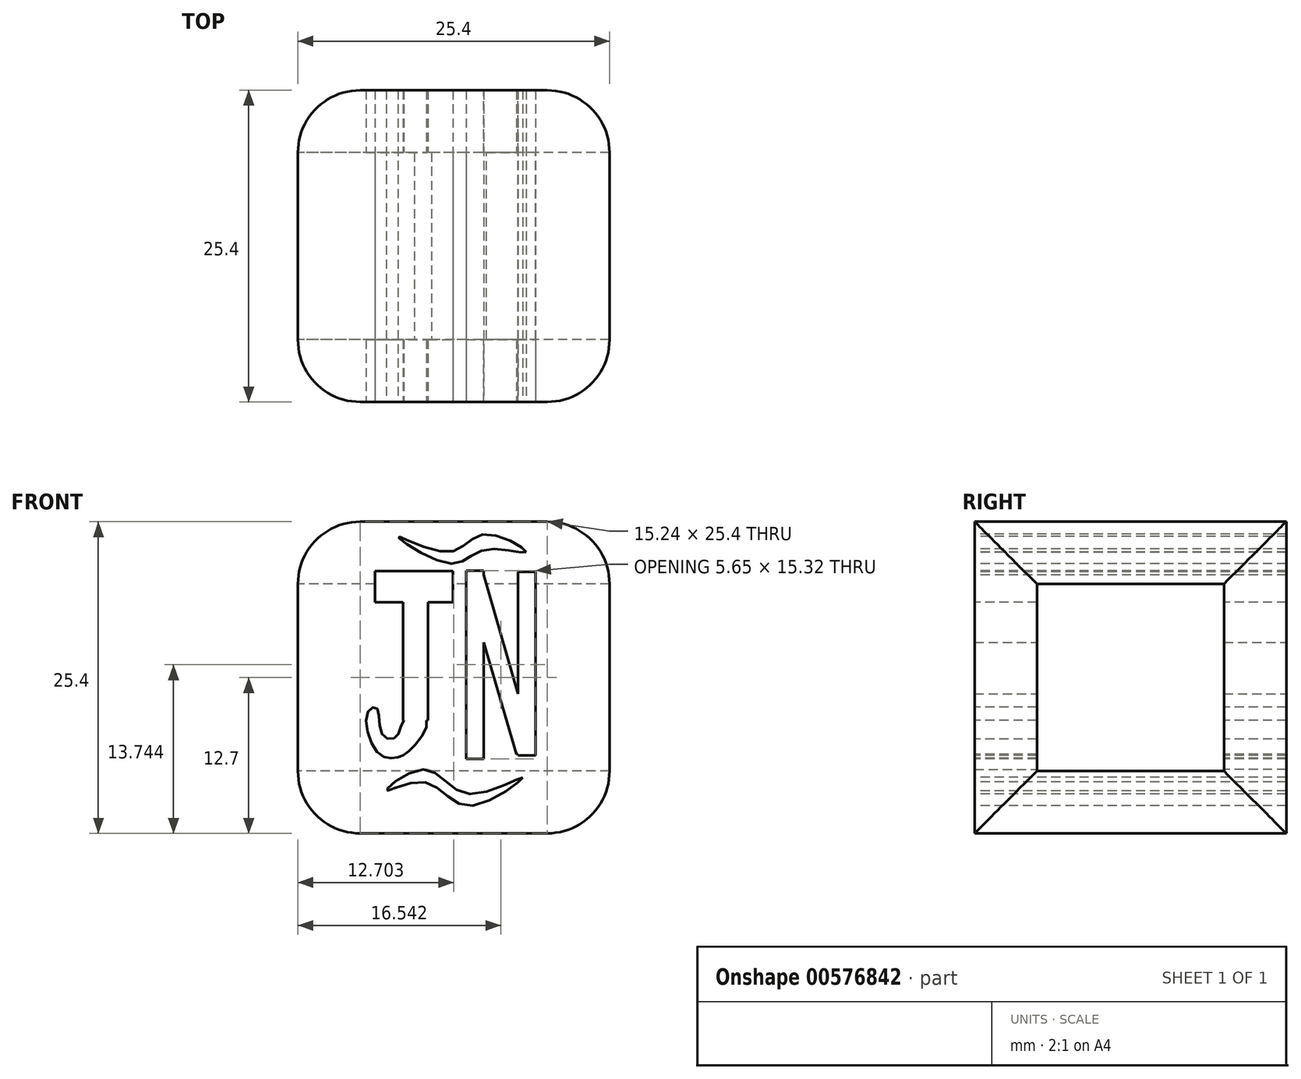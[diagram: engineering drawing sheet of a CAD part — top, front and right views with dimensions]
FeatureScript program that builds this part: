
annotation { "Feature Type Name" : "Feature", "Feature Type Description" : "" }
export const myFeature = defineFeature(function(context is Context, id is Id, definition is map)
    precondition{}
    {
        {
            var Q0;
            Q0=qCreatedBy(makeId("Front.planeOp"),FACE);
            var sketch = newSketch(context, id + "F0", { "sketchPlane" : qUnion([Q0])});
            skLineSegment(sketch, "E0.bottom", {"start": v(-49.84, 43.23) * mm, "end": v(-24.44, 43.23) * mm});
            skLineSegment(sketch, "E0.top", {"start": v(-49.84, 17.83) * mm, "end": v(-24.44, 17.83) * mm});
            skLineSegment(sketch, "E0.left", {"start": v(-49.84, 43.23) * mm, "end": v(-49.84, 17.83) * mm});
            skLineSegment(sketch, "E0.right", {"start": v(-24.44, 43.23) * mm, "end": v(-24.44, 17.83) * mm});
            skSolve(sketch);
        }
        {
            var Q0;
            Q0=makeQuery(id+"F0.imprint","IMPRINT",FACE,{"disambiguationData":[TD([[makeQuery(id+"F0.imprint","IMPRINT",EDGE,{"derivedFrom":sQuery(id+"F0.wireOp",EDGE,"E0.bottom")}),-1.0]])]});
            extrude(context, id + "F1", {"entities" : qUnion([Q0]), "depth" : 25.4 * mm, "offsetDistance" : 25.4 * mm});
        }
        {
            var Q0;
            Q0=makeQuery(id+"F1.opExtrude","SWEPT_FACE",FACE,{"disambiguationData":[OSD([sQuery(id+"F0.wireOp",EDGE,"E0.left")])]});
            var Q1;
            Q1=makeQuery(id+"F1.opExtrude","SWEPT_FACE",FACE,{"disambiguationData":[OSD([sQuery(id+"F0.wireOp",EDGE,"E0.right")])]});
            fillet(context, id + "F2", {"entities" : qUnion([Q0, Q1]), "radius" : 5.08 * mm, "tangentPropagation" : true, "allowEdgeOverflow" : false});
        }
        {
            var Q0;
            Q0=makeQuery(id+"F1.opExtrude","SWEPT_FACE",FACE,{"disambiguationData":[OSD([sQuery(id+"F0.wireOp",EDGE,"E0.left")])]});
            extrude(context, id + "F3", {"entities" : qUnion([Q0]), "operationType" : NewBodyOperationType.REMOVE, "endBound" : BoundingType.THROUGH_ALL, "oppositeDirection" : true, "depth" : 25.4 * mm, "offsetDistance" : 25.4 * mm});
        }
        {
            var Q0;
            Q0=makeQuery(id+"F1.opExtrude","CAP_FACE",FACE,{"disambiguationData":[OSD([sQuery(id+"F0.wireOp",EDGE,"E0.bottom"),sQuery(id+"F0.wireOp",EDGE,"E0.top"),sQuery(id+"F0.wireOp",EDGE,"E0.left"),sQuery(id+"F0.wireOp",EDGE,"E0.right")])],"isStart":false});
            var sketch = newSketch(context, id + "F4", { "sketchPlane" : qUnion([Q0])});
            skLineSegment(sketch, "E1.bottom", {"start": v(-43.56, 39.2) * mm, "end": v(-37.2, 39.2) * mm});
            skLineSegment(sketch, "E1.top", {"start": v(-43.56, 36.66) * mm, "end": v(-37.2, 36.66) * mm});
            skLineSegment(sketch, "E1.left", {"start": v(-43.56, 39.2) * mm, "end": v(-43.56, 36.66) * mm});
            skLineSegment(sketch, "E1.right", {"start": v(-37.2, 39.2) * mm, "end": v(-37.2, 36.66) * mm});
            skSolve(sketch);
        }
        {
            var Q0;
            Q0=makeQuery(id+"F4.imprint","IMPRINT",FACE,{"disambiguationData":[TD([[makeQuery(id+"F4.imprint","IMPRINT",EDGE,{"derivedFrom":sQuery(id+"F4.wireOp",EDGE,"E1.bottom")}),1.0]])]});
            var sketch = newSketch(context, id + "F5", { "sketchPlane" : qUnion([Q0])});
            skLineSegment(sketch, "E2.bottom", {"start": v(-41.26, 36.7) * mm, "end": v(-39.22, 36.7) * mm});
            skLineSegment(sketch, "E2.top", {"start": v(-41.26, 27.05) * mm, "end": v(-39.22, 27.05) * mm});
            skLineSegment(sketch, "E2.left", {"start": v(-41.26, 36.7) * mm, "end": v(-41.26, 27.05) * mm});
            skLineSegment(sketch, "E2.right", {"start": v(-39.22, 36.7) * mm, "end": v(-39.22, 27.05) * mm});
            skSolve(sketch);
        }
        {
            var Q0;
            Q0=makeQuery(id+"F4.imprint","IMPRINT",FACE,{"disambiguationData":[TD([[makeQuery(id+"F4.imprint","IMPRINT",EDGE,{"derivedFrom":sQuery(id+"F4.wireOp",EDGE,"E1.bottom")}),-1.0]])]});
            extrude(context, id + "F6", {"entities" : qUnion([Q0]), "operationType" : NewBodyOperationType.REMOVE, "oppositeDirection" : true, "depth" : 25.4 * mm, "offsetDistance" : 25.4 * mm});
        }
        {
            var Q0;
            {var subQ0=sQuery(id+"F5.wireOp",EDGE,"E2.top");Q0=makeQuery(id+"F5.imprint","IMPRINT",FACE,{"disambiguationData":[TD([[makeQuery(id+"F5.imprint","IMPRINT",EDGE,{"derivedFrom":subQ0}),1.0]])]});}
            extrude(context, id + "F7", {"entities" : qUnion([Q0]), "operationType" : NewBodyOperationType.REMOVE, "oppositeDirection" : true, "depth" : 25.4 * mm, "offsetDistance" : 25.4 * mm});
        }
        {
            var Q0;
            Q0=makeQuery(id+"F4.imprint","IMPRINT",FACE,{"disambiguationData":[TD([[makeQuery(id+"F4.imprint","IMPRINT",EDGE,{"derivedFrom":sQuery(id+"F4.wireOp",EDGE,"E1.bottom")}),1.0]])]});
            var sketch = newSketch(context, id + "F8", { "sketchPlane" : qUnion([Q0])});
            skFitSpline(sketch, "E3", {"points": [v(-39.38, 27.07) * mm, v(-41.1, 27.17) * mm, v(-41.77, 25.73) * mm, v(-42.92, 25.83) * mm, v(-43.4, 28.03) * mm, v(-44.17, 27.65) * mm, v(-43.3, 24.4) * mm, v(-41.77, 24) * mm, v(-40.53, 24.77) * mm, v(-39.38, 27.07) * mm]});
            skSolve(sketch);
        }
        {
            var Q0;
            Q0=makeQuery(id+"F4.imprint","IMPRINT",FACE,{"disambiguationData":[TD([[makeQuery(id+"F4.imprint","IMPRINT",EDGE,{"derivedFrom":sQuery(id+"F4.wireOp",EDGE,"E1.bottom")}),1.0]])]});
            var sketch = newSketch(context, id + "F9", { "sketchPlane" : qUnion([Q0])});
            skLineSegment(sketch, "E4.bottom", {"start": v(-36.12, 39.24) * mm, "end": v(-34.69, 39.24) * mm});
            skLineSegment(sketch, "E4.top", {"start": v(-36.12, 23.91) * mm, "end": v(-34.69, 23.91) * mm});
            skLineSegment(sketch, "E4.left", {"start": v(-36.12, 39.24) * mm, "end": v(-36.12, 23.91) * mm});
            skLineSegment(sketch, "E4.right", {"start": v(-34.69, 39.24) * mm, "end": v(-34.69, 23.91) * mm});
            skSolve(sketch);
        }
        {
            var Q0;
            Q0=makeQuery(id+"F4.imprint","IMPRINT",FACE,{"disambiguationData":[TD([[makeQuery(id+"F4.imprint","IMPRINT",EDGE,{"derivedFrom":sQuery(id+"F4.wireOp",EDGE,"E1.bottom")}),1.0]])]});
            var sketch = newSketch(context, id + "F10", { "sketchPlane" : qUnion([Q0])});
            skLineSegment(sketch, "E5", {"start": v(-34.77, 39.16) * mm, "end": v(-35.9, 37.55) * mm});
            skLineSegment(sketch, "E6", {"start": v(-35.9, 37.55) * mm, "end": v(-32.02, 24.27) * mm});
            skLineSegment(sketch, "E7", {"start": v(-32.02, 24.27) * mm, "end": v(-30.5, 24.27) * mm});
            skLineSegment(sketch, "E8", {"start": v(-30.5, 24.27) * mm, "end": v(-34.77, 39.16) * mm});
            skSolve(sketch);
        }
        {
            var Q0;
            Q0=makeQuery(id+"F4.imprint","IMPRINT",FACE,{"disambiguationData":[TD([[makeQuery(id+"F4.imprint","IMPRINT",EDGE,{"derivedFrom":sQuery(id+"F4.wireOp",EDGE,"E1.bottom")}),1.0]])]});
            var sketch = newSketch(context, id + "F11", { "sketchPlane" : qUnion([Q0])});
            skLineSegment(sketch, "E9.bottom", {"start": v(-31.9, 24.2) * mm, "end": v(-30.47, 24.2) * mm});
            skLineSegment(sketch, "E9.top", {"start": v(-31.9, 39.14) * mm, "end": v(-30.47, 39.14) * mm});
            skLineSegment(sketch, "E9.left", {"start": v(-31.9, 24.2) * mm, "end": v(-31.9, 39.14) * mm});
            skLineSegment(sketch, "E9.right", {"start": v(-30.47, 24.2) * mm, "end": v(-30.47, 39.14) * mm});
            skSolve(sketch);
        }
        {
            var Q0;
            Q0=makeQuery(id+"F10.imprint","IMPRINT",FACE,{"disambiguationData":[TD([[makeQuery(id+"F10.imprint","IMPRINT",EDGE,{"derivedFrom":sQuery(id+"F10.wireOp",EDGE,"E5")}),1.0]])]});
            extrude(context, id + "F12", {"entities" : qUnion([Q0]), "operationType" : NewBodyOperationType.REMOVE, "oppositeDirection" : true, "depth" : 25.4 * mm, "offsetDistance" : 25.4 * mm});
        }
        {
            var Q0;
            Q0=makeQuery(id+"F11.imprint","IMPRINT",FACE,{"disambiguationData":[TD([[makeQuery(id+"F11.imprint","IMPRINT",EDGE,{"derivedFrom":sQuery(id+"F11.wireOp",EDGE,"E9.bottom")}),1.0]])]});
            extrude(context, id + "F13", {"entities" : qUnion([Q0]), "operationType" : NewBodyOperationType.REMOVE, "oppositeDirection" : true, "depth" : 25.4 * mm, "offsetDistance" : 25.4 * mm});
        }
        {
            var Q0;
            Q0=makeQuery(id+"F9.imprint","IMPRINT",FACE,{"disambiguationData":[TD([[makeQuery(id+"F9.imprint","IMPRINT",EDGE,{"derivedFrom":sQuery(id+"F9.wireOp",EDGE,"E4.bottom")}),-1.0]])]});
            extrude(context, id + "F14", {"entities" : qUnion([Q0]), "operationType" : NewBodyOperationType.REMOVE, "oppositeDirection" : true, "depth" : 25.4 * mm, "offsetDistance" : 25.4 * mm});
        }
        {
            var Q0;
            Q0=makeQuery(id+"F8.imprint","IMPRINT",FACE,{"disambiguationData":[TD([[makeQuery(id+"F8.imprint","IMPRINT",EDGE,{"derivedFrom":sQuery(id+"F8.wireOp",EDGE,"E3")}),1.0]])]});
            extrude(context, id + "F15", {"entities" : qUnion([Q0]), "operationType" : NewBodyOperationType.REMOVE, "oppositeDirection" : true, "depth" : 25.4 * mm, "offsetDistance" : 25.4 * mm});
        }
        {
            var Q0;
            Q0=makeQuery(id+"F4.imprint","IMPRINT",FACE,{"disambiguationData":[TD([[makeQuery(id+"F4.imprint","IMPRINT",EDGE,{"derivedFrom":sQuery(id+"F4.wireOp",EDGE,"E1.bottom")}),1.0]])]});
            var sketch = newSketch(context, id + "F16", { "sketchPlane" : qUnion([Q0])});
            skFitSpline(sketch, "E10", {"points": [v(-31.53, 22.38) * mm, v(-35.93, 21.04) * mm, v(-39.57, 23.05) * mm, v(-42.63, 21.33) * mm, v(-39.57, 22) * mm, v(-35.84, 20.08) * mm, v(-31.53, 22.38) * mm]});
            skSolve(sketch);
        }
        {
            var Q0;
            Q0=makeQuery(id+"F16.imprint","IMPRINT",FACE,{"disambiguationData":[TD([[makeQuery(id+"F16.imprint","IMPRINT",EDGE,{"derivedFrom":sQuery(id+"F16.wireOp",EDGE,"E10")}),1.0]])]});
            extrude(context, id + "F17", {"entities" : qUnion([Q0]), "operationType" : NewBodyOperationType.REMOVE, "oppositeDirection" : true, "depth" : 25.4 * mm, "offsetDistance" : 25.4 * mm});
        }
        {
            var Q0;
            Q0=makeQuery(id+"F4.imprint","IMPRINT",FACE,{"disambiguationData":[TD([[makeQuery(id+"F4.imprint","IMPRINT",EDGE,{"derivedFrom":sQuery(id+"F4.wireOp",EDGE,"E1.bottom")}),1.0]])]});
            var sketch = newSketch(context, id + "F18", { "sketchPlane" : qUnion([Q0])});
            skFitSpline(sketch, "E11", {"points": [v(-31.24, 40.77) * mm, v(-34.6, 42.2) * mm, v(-37.56, 40.77) * mm, v(-41.68, 42.01) * mm, v(-37.46, 39.8) * mm, v(-34.5, 40.96) * mm, v(-31.24, 40.77) * mm]});
            skSolve(sketch);
        }
        {
            var Q0;
            Q0=makeQuery(id+"F18.imprint","IMPRINT",FACE,{"disambiguationData":[TD([[makeQuery(id+"F18.imprint","IMPRINT",EDGE,{"derivedFrom":sQuery(id+"F18.wireOp",EDGE,"E11")}),1.0]])]});
            extrude(context, id + "F19", {"entities" : qUnion([Q0]), "operationType" : NewBodyOperationType.REMOVE, "oppositeDirection" : true, "depth" : 25.4 * mm, "offsetDistance" : 25.4 * mm});
        }
    });
